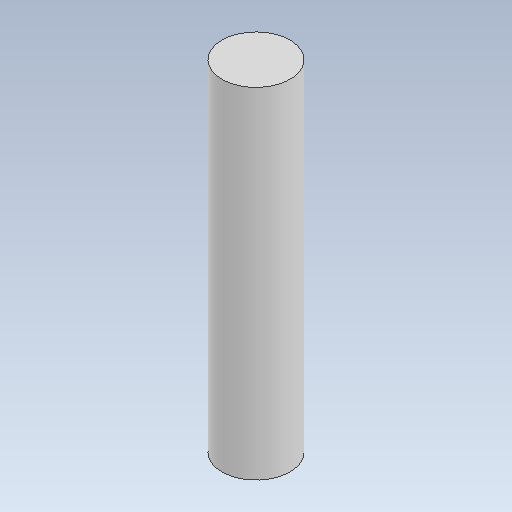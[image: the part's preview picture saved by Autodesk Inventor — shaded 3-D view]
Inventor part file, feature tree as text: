
AUTODESK INVENTOR PART (.ipt)
format: ipt  version: 2023 (Build 270158000, 158)  size: 79,360 bytes
history: native  units: mm
features: extrude x1, sketch x1
ambient origin geometry x8: Origin, YZ Plane, XZ Plane, XY Plane, X Axis, Y Axis, Z Axis, Center Point
bodies: Solid1 (feature_tree)
feature tree (2):
  extrude  "Extrusion1"  Depth=15.0mm TaperAngle=0.0deg
  sketch  "Sketch1"  dims[d0=3.0mm d1=15.0mm d2=0.0mm]
